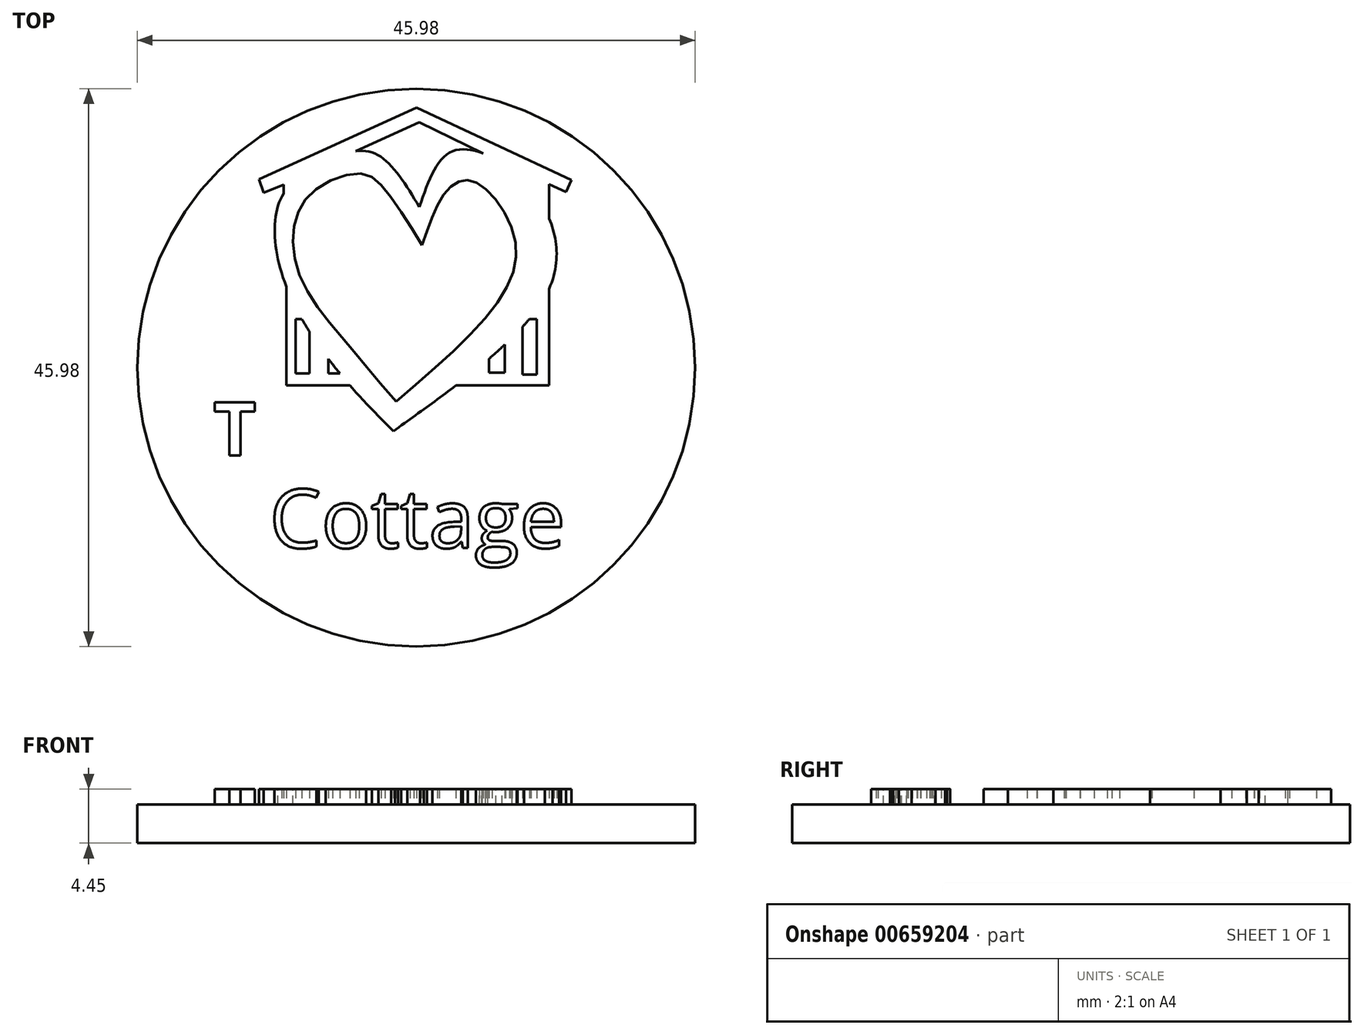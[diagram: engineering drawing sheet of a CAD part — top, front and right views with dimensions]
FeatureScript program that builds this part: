
annotation { "Feature Type Name" : "Feature", "Feature Type Description" : "" }
export const myFeature = defineFeature(function(context is Context, id is Id, definition is map)
    precondition{}
    {
        {
            var Q0;
            Q0=qCreatedBy(makeId("Top.planeOp"),FACE);
            var sketch = newSketch(context, id + "F0", { "sketchPlane" : qUnion([Q0])});
            skCircle(sketch, "E0", {"center": v(0, 0) * mm, "radius": 22.99 * mm});
            skSolve(sketch);
        }
        {
            var Q0;
            Q0=qSketchRegion(id+"F0",true);
            extrude(context, id + "F1", {"entities" : qUnion([Q0]), "depth" : 6.35 * mm, "offsetDistance" : 25.4 * mm});
        }
        {
            var Q0;
            Q0=makeQuery(id+"F1.opExtrude","CAP_FACE",FACE,{"disambiguationData":[OSD([sQuery(id+"F0.wireOp",EDGE,"E0")])],"isStart":false});
            var sketch = newSketch(context, id + "F2", { "sketchPlane" : qUnion([Q0])});
            skCircle(sketch, "E1", {"center": v(0, 0) * mm, "radius": 22.23 * mm});
            skSolve(sketch);
        }
        {
            var Q0;
            Q0=qSketchRegion(id+"F2",true);
            extrude(context, id + "F3", {"entities" : qUnion([Q0]), "operationType" : NewBodyOperationType.REMOVE, "oppositeDirection" : true, "depth" : 3.17 * mm, "offsetDistance" : 25.4 * mm});
        }
        {
            var Q0;
            {var subQ0=sQuery(id+"F2.wireOp",EDGE,"E1");Q0=makeQuery(id+"FgJwaarcNfyRxLp_1.boolean.opBoolean","SPLIT",FACE,{"disambiguationData":[TD([makeQuery(id+"F3.boolean.opBoolean","COPY",FACE,{"derivedFrom":makeQuery(id+"F3.opExtrude","SWEPT_FACE",FACE,{"disambiguationData":[OSD([subQ0])]})})])],"derivedFrom":makeQuery(id+"F3.boolean.opBoolean","COPY",FACE,{"derivedFrom":makeQuery(id+"F3.opExtrude","CAP_FACE",FACE,{"disambiguationData":[OSD([subQ0])],"isStart":false})})});}
            var sketch = newSketch(context, id + "F4", { "sketchPlane" : qUnion([Q0])});
            skLineSegment(sketch, "E2.bottom", {"start": v(-13.19, -10.66) * mm, "end": v(10.78, -10.66) * mm});
            skLineSegment(sketch, "E2.top", {"start": v(-13.19, 7.53) * mm, "end": v(10.78, 7.53) * mm});
            skLineSegment(sketch, "E2.left", {"start": v(-13.19, -10.66) * mm, "end": v(-13.19, 7.53) * mm});
            skLineSegment(sketch, "E2.right", {"start": v(10.78, -10.66) * mm, "end": v(10.78, 7.53) * mm});
            skLineSegment(sketch, "E3", {"start": v(-13.19, -3.67) * mm, "end": v(5.88, -3.67) * mm});
            skLineSegment(sketch, "E4.bottom", {"start": v(-12.1, -4.76) * mm, "end": v(-10.9, -4.76) * mm});
            skLineSegment(sketch, "E4.top", {"start": v(-12.1, -9.45) * mm, "end": v(-10.9, -9.45) * mm});
            skLineSegment(sketch, "E4.left", {"start": v(-12.1, -4.76) * mm, "end": v(-12.1, -9.45) * mm});
            skLineSegment(sketch, "E4.right", {"start": v(-10.9, -4.76) * mm, "end": v(-10.9, -9.45) * mm});
            skLineSegment(sketch, "E5.1.0.0", {"start": v(-7.98, -4.76) * mm, "end": v(-7.98, -9.45) * mm});
            skLineSegment(sketch, "E5.1.0.1", {"start": v(-9.18, -4.76) * mm, "end": v(-9.18, -9.45) * mm});
            skLineSegment(sketch, "E5.1.0.2", {"start": v(-9.18, -4.76) * mm, "end": v(-7.98, -4.76) * mm});
            skLineSegment(sketch, "E5.1.0.3", {"start": v(-9.18, -9.45) * mm, "end": v(-7.98, -9.45) * mm});
            skLineSegment(sketch, "E5.2.0.0", {"start": v(-5.06, -4.76) * mm, "end": v(-5.06, -9.45) * mm});
            skLineSegment(sketch, "E5.2.0.1", {"start": v(-6.26, -4.76) * mm, "end": v(-6.26, -9.45) * mm});
            skLineSegment(sketch, "E5.2.0.2", {"start": v(-6.26, -4.76) * mm, "end": v(-5.06, -4.76) * mm});
            skLineSegment(sketch, "E5.2.0.3", {"start": v(-6.26, -9.45) * mm, "end": v(-5.06, -9.45) * mm});
            skLineSegment(sketch, "E5.3.0.0", {"start": v(-2.13, -4.76) * mm, "end": v(-2.13, -9.45) * mm});
            skLineSegment(sketch, "E5.3.0.1", {"start": v(-3.34, -4.76) * mm, "end": v(-3.34, -9.45) * mm});
            skLineSegment(sketch, "E5.3.0.2", {"start": v(-3.34, -4.76) * mm, "end": v(-2.13, -4.76) * mm});
            skLineSegment(sketch, "E5.3.0.3", {"start": v(-3.34, -9.45) * mm, "end": v(-2.13, -9.45) * mm});
            skLineSegment(sketch, "E5.4.0.0", {"start": v(0.79, -4.76) * mm, "end": v(0.79, -9.45) * mm});
            skLineSegment(sketch, "E5.4.0.1", {"start": v(-0.42, -4.76) * mm, "end": v(-0.42, -9.45) * mm});
            skLineSegment(sketch, "E5.4.0.2", {"start": v(-0.42, -4.76) * mm, "end": v(0.79, -4.76) * mm});
            skLineSegment(sketch, "E5.4.0.3", {"start": v(-0.42, -9.45) * mm, "end": v(0.79, -9.45) * mm});
            skLineSegment(sketch, "E5.5.0.0", {"start": v(3.7, -4.76) * mm, "end": v(3.7, -9.45) * mm});
            skLineSegment(sketch, "E5.5.0.1", {"start": v(2.5, -4.76) * mm, "end": v(2.5, -9.45) * mm});
            skLineSegment(sketch, "E5.5.0.2", {"start": v(2.5, -4.76) * mm, "end": v(3.7, -4.76) * mm});
            skLineSegment(sketch, "E5.5.0.3", {"start": v(2.5, -9.45) * mm, "end": v(3.7, -9.45) * mm});
            skLineSegment(sketch, "E5.6.0.0", {"start": v(6.63, -4.76) * mm, "end": v(6.63, -9.45) * mm});
            skLineSegment(sketch, "E5.6.0.1", {"start": v(5.42, -4.76) * mm, "end": v(5.42, -9.45) * mm});
            skLineSegment(sketch, "E5.6.0.2", {"start": v(5.42, -4.76) * mm, "end": v(6.63, -4.76) * mm});
            skLineSegment(sketch, "E5.6.0.3", {"start": v(5.42, -9.45) * mm, "end": v(6.63, -9.45) * mm});
            skLineSegment(sketch, "E5.7.0.0", {"start": v(9.55, -4.76) * mm, "end": v(9.55, -9.45) * mm});
            skLineSegment(sketch, "E5.7.0.1", {"start": v(8.35, -4.76) * mm, "end": v(8.35, -9.45) * mm});
            skLineSegment(sketch, "E5.7.0.2", {"start": v(8.35, -4.76) * mm, "end": v(9.55, -4.76) * mm});
            skLineSegment(sketch, "E5.7.0.3", {"start": v(8.35, -9.45) * mm, "end": v(9.55, -9.45) * mm});
            skLineSegment(sketch, "E5.direction1", {"start": v(-12.1, -9.45) * mm, "end": v(-9.18, -9.45) * mm, "construction": true});
            skLineSegment(sketch, "E6.bottom", {"start": v(-12.17, 6.62) * mm, "end": v(-8.3, 6.62) * mm});
            skLineSegment(sketch, "E6.left", {"start": v(-12.17, 6.62) * mm, "end": v(-12.17, -2.73) * mm});
            skLineSegment(sketch, "E6.right", {"start": v(-8.3, 6.62) * mm, "end": v(-8.3, -2.73) * mm});
            skLineSegment(sketch, "E7.bottom", {"start": v(-5.74, -2.71) * mm, "end": v(2.53, -2.71) * mm});
            skLineSegment(sketch, "E7.top", {"start": v(-6.82, 6.64) * mm, "end": v(3.57, 6.64) * mm});
            skLineSegment(sketch, "E7.left", {"start": v(-6.82, -2.71) * mm, "end": v(-6.82, 6.64) * mm});
            skLineSegment(sketch, "E7.right", {"start": v(3.57, -2.71) * mm, "end": v(3.57, 6.64) * mm});
            skLineSegment(sketch, "E8", {"start": v(9.5, -3.67) * mm, "end": v(9.5, 6.64) * mm});
            skLineSegment(sketch, "E9", {"start": v(9.5, 6.64) * mm, "end": v(4.68, 6.64) * mm});
            skLineSegment(sketch, "E10", {"start": v(4.68, 6.64) * mm, "end": v(4.68, -2.71) * mm});
            skLineSegment(sketch, "E11", {"start": v(5.88, -3.67) * mm, "end": v(5.88, 5.32) * mm});
            skLineSegment(sketch, "E12", {"start": v(5.88, 5.32) * mm, "end": v(8.29, 5.32) * mm});
            skLineSegment(sketch, "E13", {"start": v(8.29, 5.32) * mm, "end": v(8.35, -3.67) * mm});
            skLineSegment(sketch, "E14.trimOffspring", {"start": v(8.35, -3.67) * mm, "end": v(10.78, -3.67) * mm});
            skLineSegment(sketch, "E15", {"start": v(-12.17, -2.73) * mm, "end": v(-13.19, -2.73) * mm});
            skLineSegment(sketch, "E16", {"start": v(-8.3, -2.73) * mm, "end": v(-6.82, -2.71) * mm});
            skPoint(sketch, "E17.orphan", {"position": v(4.68, -3.67) * mm});
            skLineSegment(sketch, "E18", {"start": v(4.68, -2.71) * mm, "end": v(3.57, -2.71) * mm});
            skLineSegment(sketch, "E19.bottom", {"start": v(11.97, -7.87) * mm, "end": v(15.92, -7.87) * mm});
            skLineSegment(sketch, "E19.top", {"start": v(11.97, -11.38) * mm, "end": v(15.92, -11.38) * mm});
            skLineSegment(sketch, "E19.left", {"start": v(11.97, -7.87) * mm, "end": v(11.97, -11.38) * mm});
            skLineSegment(sketch, "E19.right", {"start": v(15.92, -7.87) * mm, "end": v(15.92, -11.38) * mm});
            skLineSegment(sketch, "E20.top", {"start": v(-5.74, 1.06) * mm, "end": v(2.53, 1.06) * mm});
            skLineSegment(sketch, "E20.left", {"start": v(-5.74, -2.71) * mm, "end": v(-5.74, 1.06) * mm});
            skLineSegment(sketch, "E20.right", {"start": v(2.53, -2.71) * mm, "end": v(2.53, 1.06) * mm});
            skLineSegment(sketch, "E21.bottom", {"start": v(-5.74, 2.08) * mm, "end": v(2.45, 2.08) * mm});
            skLineSegment(sketch, "E21.top", {"start": v(-5.74, 5.74) * mm, "end": v(2.45, 5.74) * mm});
            skLineSegment(sketch, "E21.left", {"start": v(-5.74, 2.08) * mm, "end": v(-5.74, 5.74) * mm});
            skLineSegment(sketch, "E21.right", {"start": v(2.45, 2.08) * mm, "end": v(2.45, 5.74) * mm});
            skLineSegment(sketch, "E22", {"start": v(-13.19, 7.53) * mm, "end": v(-1.2, 13.11) * mm});
            skLineSegment(sketch, "E23", {"start": v(10.78, 7.53) * mm, "end": v(-1.2, 13.11) * mm});
            skLineSegment(sketch, "E24", {"start": v(-13.19, 7.53) * mm, "end": v(-14.89, 6.73) * mm});
            skLineSegment(sketch, "E25", {"start": v(-15.38, 7.8) * mm, "end": v(-1.24, 14.38) * mm});
            skLineSegment(sketch, "E26", {"start": v(-1.24, 14.38) * mm, "end": v(12.81, 7.83) * mm});
            skLineSegment(sketch, "E27", {"start": v(10.78, 7.53) * mm, "end": v(12.33, 6.8) * mm});
            skLineSegment(sketch, "E28", {"start": v(12.81, 7.83) * mm, "end": v(12.33, 6.8) * mm});
            skLineSegment(sketch, "E29", {"start": v(-14.89, 6.73) * mm, "end": v(-15.38, 7.8) * mm});
            skSolve(sketch);
        }
        {
            var Q0;
            Q0=qCreatedBy(makeId("Top.planeOp"),FACE);
            var sketch = newSketch(context, id + "F5", { "sketchPlane" : qUnion([Q0])});
            skCircle(sketch, "E30", {"center": v(0, 0) * mm, "radius": 23.37 * mm});
            skCircle(sketch, "E31", {"center": v(0, 0) * mm, "radius": 24.13 * mm});
            skSolve(sketch);
        }
        {
            var Q0;
            Q0=qSketchRegion(id+"F5",true);
            extrude(context, id + "F6", {"entities" : qUnion([Q0]), "depth" : 25.4 * mm, "offsetDistance" : 25.4 * mm});
        }
        {
            var Q0;
            Q0=makeQuery(id+"F6.opExtrude","SWEPT_BODY",BODY,{"disambiguationData":[OSD([sQuery(id+"F5.wireOp",EDGE,"E30"),sQuery(id+"F5.wireOp",EDGE,"E31")])]});
            transform(context, id + "F7", {"entities" : qUnion([Q0]), "transformType" : TransformType.TRANSLATION_3D, "dx" : 0 * mm, "dy" : 0 * mm, "dz" : 0 * mm, "makeCopy" : true});
        }
        {
            var Q0;
            Q0=makeQuery(id+"F7.opPattern","COPY",BODY,{"derivedFrom":makeQuery(id+"F6.opExtrude","SWEPT_BODY",BODY,{"disambiguationData":[OSD([sQuery(id+"F5.wireOp",EDGE,"E30"),sQuery(id+"F5.wireOp",EDGE,"E31")])]}),"instanceName":"1"});
            var Q1;
            Q1=makeQuery(id+"F6.opExtrude","SWEPT_BODY",BODY,{"disambiguationData":[OSD([sQuery(id+"F5.wireOp",EDGE,"E30"),sQuery(id+"F5.wireOp",EDGE,"E31")])]});
            deleteBodies(context, id + "F8", {"entities" : qUnion([Q0, Q1])});
        }
        {
            var Q0;
            {var subQ4=sQuery(id+"F4.wireOp",EDGE,"E2.bottom");Q0=makeQuery(id+"F4.imprint","IMPRINT",FACE,{"disambiguationData":[TD([[makeQuery(id+"F4.imprint","IMPRINT",EDGE,{"derivedFrom":subQ4}),-1.0]])]});}
            var sketch = newSketch(context, id + "F9", { "sketchPlane" : qUnion([Q0])});
            skLineSegment(sketch, "E32", {"start": v(-12.96, 15.52) * mm, "end": v(0.03, 21.44) * mm});
            skLineSegment(sketch, "E33", {"start": v(0.03, 21.44) * mm, "end": v(12.8, 15.46) * mm});
            skLineSegment(sketch, "E34", {"start": v(12.8, 15.46) * mm, "end": v(12.33, 14.46) * mm});
            skLineSegment(sketch, "E35", {"start": v(12.33, 14.46) * mm, "end": v(10.95, 15.11) * mm});
            skLineSegment(sketch, "E36", {"start": v(10.95, -1.47) * mm, "end": v(3.26, -1.47) * mm});
            skLineSegment(sketch, "E37", {"start": v(-10.93, 15.08) * mm, "end": v(-12.57, 14.42) * mm});
            skLineSegment(sketch, "E38", {"start": v(-12.57, 14.42) * mm, "end": v(-12.96, 15.52) * mm});
            skLineSegment(sketch, "E39.bottom", {"start": v(-9.96, 4) * mm, "end": v(-9.43, 4) * mm});
            skLineSegment(sketch, "E39.top", {"start": v(-9.96, -0.47) * mm, "end": v(-8.82, -0.47) * mm});
            skLineSegment(sketch, "E39.left", {"start": v(-9.96, 4) * mm, "end": v(-9.96, -0.47) * mm});
            skLineSegment(sketch, "E39.right", {"start": v(-8.82, 2.99) * mm, "end": v(-8.82, -0.47) * mm});
            skLineSegment(sketch, "E40.top", {"start": v(-7.26, -0.47) * mm, "end": v(-6.16, -0.47) * mm});
            skLineSegment(sketch, "E40.left", {"start": v(-7.26, 0.74) * mm, "end": v(-7.26, -0.47) * mm});
            skLineSegment(sketch, "E41.top", {"start": v(6, -0.41) * mm, "end": v(7.3, -0.41) * mm});
            skLineSegment(sketch, "E41.left", {"start": v(6, 0.73) * mm, "end": v(6, -0.41) * mm});
            skLineSegment(sketch, "E41.right", {"start": v(7.3, 1.9) * mm, "end": v(7.3, -0.41) * mm});
            skLineSegment(sketch, "E42.bottom", {"start": v(9.32, 4) * mm, "end": v(9.95, 4) * mm});
            skLineSegment(sketch, "E42.top", {"start": v(8.75, -0.57) * mm, "end": v(9.95, -0.57) * mm});
            skLineSegment(sketch, "E42.left", {"start": v(8.75, 3.36) * mm, "end": v(8.75, -0.57) * mm});
            skLineSegment(sketch, "E42.right", {"start": v(9.95, 4) * mm, "end": v(9.95, -0.57) * mm});
            skFitSpline(sketch, "E43", {"points": [v(-1.88, -5.23) * mm, v(-5.46, -1.47) * mm, v(-10.7, 6.66) * mm, v(-11.17, 13.93) * mm, v(-7.7, 16.87) * mm, v(-3.6, 17.73) * mm, v(0.25, 13.24) * mm], "startDerivative": vector(-21.35, 21.53) * mm, "endDerivative": vector(21.52, -36.05) * mm});
            skPoint(sketch, "E44.3.internal.snap0", {"position": v(7.3, 1.8) * mm});
            skFitSpline(sketch, "E44", {"points": [v(-1.88, -5.23) * mm, v(10.94, 6.49) * mm, v(10.78, 12.68) * mm, v(7.3, 16.69) * mm, v(2.95, 17.83) * mm, v(0.25, 13.24) * mm], "startDerivative": vector(53.54, 38.35) * mm, "endDerivative": vector(-12.06, -35) * mm});
            skLineSegment(sketch, "E45", {"start": v(10.95, 15.11) * mm, "end": v(10.95, 12.3) * mm});
            skLineSegment(sketch, "E46", {"start": v(-10.93, 15.08) * mm, "end": v(-10.93, 14.37) * mm});
            skLineSegment(sketch, "E47", {"start": v(-10.7, -1.47) * mm, "end": v(-10.7, 6.66) * mm});
            skLineSegment(sketch, "E48", {"start": v(10.95, -1.47) * mm, "end": v(10.94, 6.49) * mm});
            skPoint(sketch, "E49.orphan", {"position": v(7.3, 4) * mm});
            skLineSegment(sketch, "E50", {"start": v(-4.98, 17.85) * mm, "end": v(0.25, 20.23) * mm});
            skLineSegment(sketch, "E51", {"start": v(0.25, 20.23) * mm, "end": v(5.52, 17.64) * mm});
            skFitSpline(sketch, "E52", {"points": [v(0.46, 10.11) * mm, v(-2.63, 14.72) * mm, v(-4.58, 16) * mm, v(-8.35, 14.64) * mm, v(-10.04, 11.76) * mm, v(-9.53, 7.4) * mm, v(-6.27, 2.66) * mm, v(-1.66, -2.8) * mm], "startDerivative": vector(-17.2, 30.8) * mm, "endDerivative": vector(31.6, -36.39) * mm});
            skFitSpline(sketch, "E53", {"points": [v(0.46, 10.11) * mm, v(2.06, 13.96) * mm, v(3.72, 15.4) * mm, v(5.58, 14.85) * mm, v(8.12, 10.66) * mm, v(6.85, 5.58) * mm, v(-1.66, -2.8) * mm], "startDerivative": vector(10.2, 26.33) * mm, "endDerivative": vector(-37.61, -32.15) * mm});
            skLineSegment(sketch, "E54.trimOffspring", {"start": v(-5.46, -1.47) * mm, "end": v(-10.7, -1.47) * mm});
            skText(sketch, "E55", { "text": "T", "fontName": "OpenSans-Bold.ttf"});
            skText(sketch, "E56", { "text": "Cottage", "fontName": "OpenSans-Regular.ttf"});
            const initialGuessF9  = {"E55": [-0.01673, -0.00723, 1, 0, 0.00442], "E56": [-0.0121, -0.01486, 1, 0, 0.00487]};
            skSetInitialGuess(sketch, initialGuessF9);
            skSolve(sketch);
        }
        {
            var Q0;
            Q0 = qSketchRegion(id + "F9", true);
            extrude(context, id + "F10", {"entities" : qUnion([Q0]), "operationType" : NewBodyOperationType.ADD, "depth" : 1.27 * mm, "offsetDistance" : 25.4 * mm});
        }
        {
            var Q0;
            {var subQ4=sQuery(id+"F4.wireOp",EDGE,"E2.bottom");Q0=makeQuery(id+"F4.imprint","IMPRINT",FACE,{"disambiguationData":[TD([[makeQuery(id+"F4.imprint","IMPRINT",EDGE,{"derivedFrom":subQ4}),-1.0]])]});}
            var sketch = newSketch(context, id + "F11", { "sketchPlane" : qUnion([Q0])});
            skCircle(sketch, "E57", {"center": v(0, 0) * mm, "radius": 22.08 * mm});
            skCircle(sketch, "E58", {"center": v(0, 0) * mm, "radius": 25.52 * mm});
            skSolve(sketch);
        }
        {
            var Q0;
            Q0 = qSketchRegion(id + "F11", true);
            extrude(context, id + "F12", {"entities" : qUnion([Q0]), "operationType" : NewBodyOperationType.REMOVE, "depth" : 25.4 * mm, "offsetDistance" : 25.4 * mm});
        }
    });
